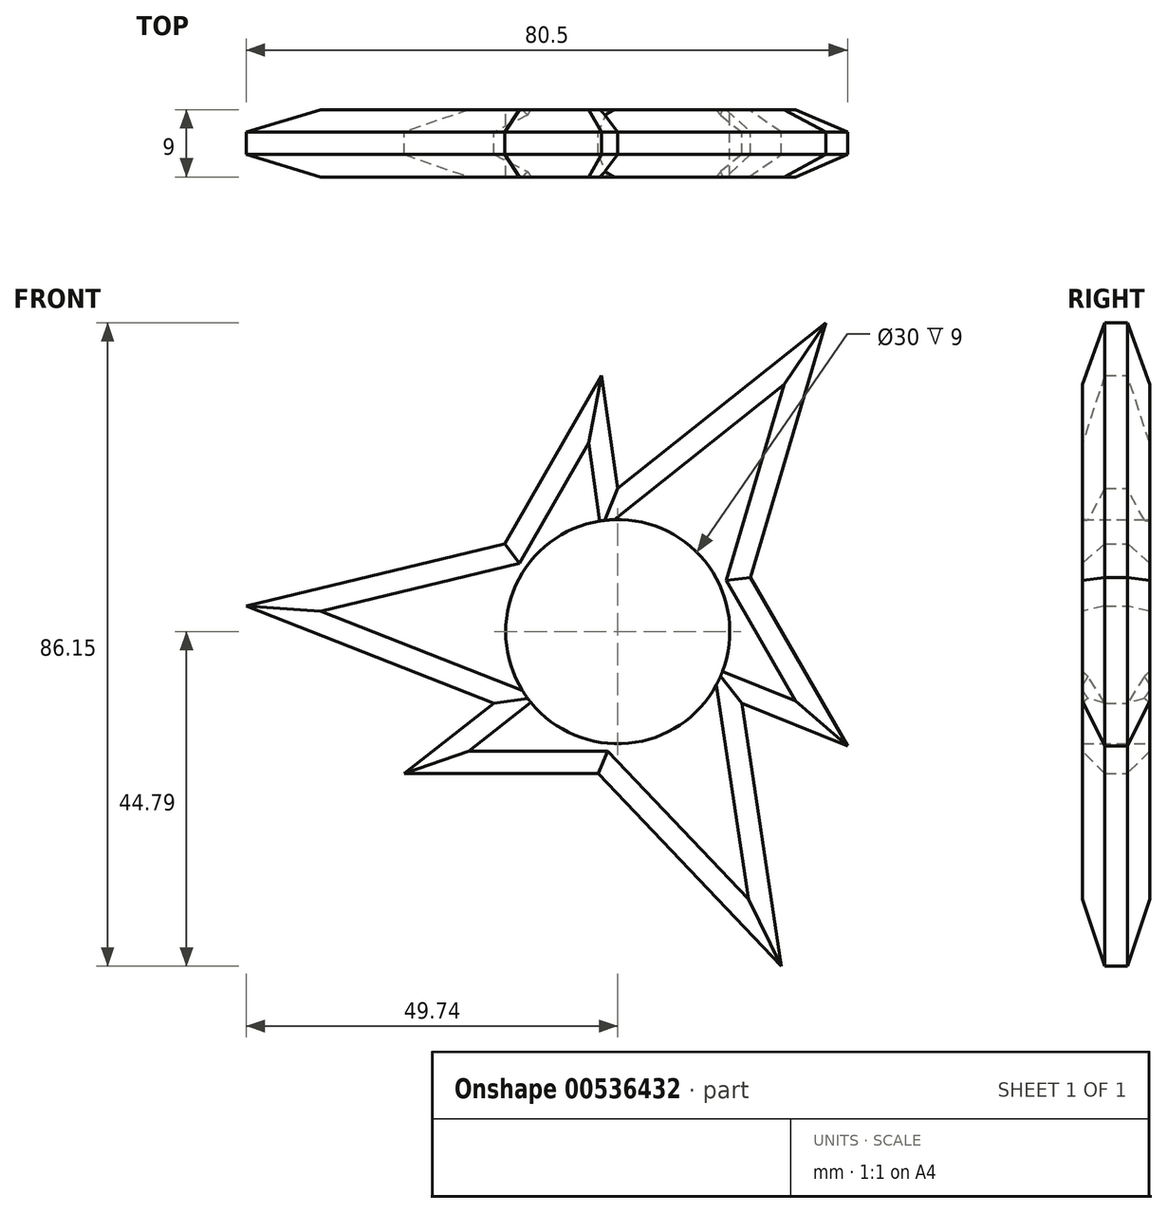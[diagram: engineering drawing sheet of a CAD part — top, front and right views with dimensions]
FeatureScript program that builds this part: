
annotation { "Feature Type Name" : "Feature", "Feature Type Description" : "" }
export const myFeature = defineFeature(function(context is Context, id is Id, definition is map)
    precondition{}
    {
        {
            var Q0;
            Q0=qCreatedBy(makeId("Front.planeOp"),FACE);
            var sketch = newSketch(context, id + "F0", { "sketchPlane" : qUnion([Q0])});
            skCircle(sketch, "E0", {"center": v(0, 0) * mm, "radius": 15 * mm});
            skCircle(sketch, "E1", {"center": v(0, 0) * mm, "radius": 19.18 * mm});
            skLineSegment(sketch, "E2", {"start": v(0, 19.18) * mm, "end": v(27.83, 41.36) * mm});
            skLineSegment(sketch, "E3", {"start": v(27.83, 41.36) * mm, "end": v(17.77, 7.22) * mm});
            skLineSegment(sketch, "E4.1.0", {"start": v(-16.61, -9.6) * mm, "end": v(-49.74, 3.42) * mm});
            skLineSegment(sketch, "E4.1.1", {"start": v(-49.74, 3.42) * mm, "end": v(-15.14, 11.78) * mm});
            skLineSegment(sketch, "E4.2.0", {"start": v(16.61, -9.6) * mm, "end": v(21.9, -44.79) * mm});
            skLineSegment(sketch, "E4.2.1", {"start": v(21.9, -44.79) * mm, "end": v(-2.63, -19) * mm});
            skLineSegment(sketch, "E5", {"start": v(-16.61, -9.6) * mm, "end": v(-28.62, -19) * mm});
            skLineSegment(sketch, "E6", {"start": v(-28.62, -19) * mm, "end": v(-2.63, -19) * mm});
            skLineSegment(sketch, "E7.1.0", {"start": v(16.61, -9.6) * mm, "end": v(30.76, -15.28) * mm});
            skLineSegment(sketch, "E7.1.1", {"start": v(30.76, -15.28) * mm, "end": v(17.77, 7.22) * mm});
            skLineSegment(sketch, "E7.2.0", {"start": v(0, 19.18) * mm, "end": v(-2.15, 34.28) * mm});
            skLineSegment(sketch, "E7.2.1", {"start": v(-2.15, 34.28) * mm, "end": v(-15.14, 11.78) * mm});
            skSolve(sketch);
        }
        {
            var Q0;
            {var subQ0=sQuery(id+"F0.wireOp",EDGE,"E4.1.0");Q0=makeQuery(id+"F0.imprint","IMPRINT",FACE,{"disambiguationData":[TD([[makeQuery(id+"F0.imprint","IMPRINT",EDGE,{"derivedFrom":subQ0}),-1.0]])]});}
            var Q1;
            {var subQ0=sQuery(id+"F0.wireOp",EDGE,"E2");Q1=makeQuery(id+"F0.imprint","IMPRINT",FACE,{"disambiguationData":[TD([[makeQuery(id+"F0.imprint","IMPRINT",EDGE,{"derivedFrom":subQ0}),-1.0]])]});}
            var Q2;
            {var subQ0=sQuery(id+"F0.wireOp",EDGE,"E4.2.0");Q2=makeQuery(id+"F0.imprint","IMPRINT",FACE,{"disambiguationData":[TD([[makeQuery(id+"F0.imprint","IMPRINT",EDGE,{"derivedFrom":subQ0}),-1.0]])]});}
            var Q3;
            Q3=makeQuery(id+"F0.imprint","IMPRINT",FACE,{"disambiguationData":[TD([[makeQuery(id+"F0.imprint","IMPRINT",EDGE,{"derivedFrom":sQuery(id+"F0.wireOp",EDGE,"E0")}),-1.0]])]});
            extrude(context, id + "F1", {"entities" : qUnion([Q0, Q1, Q2, Q3]), "depth" : 9 * mm, "offsetDistance" : 25 * mm});
        }
        {
            var Q0;
            Q0 = qSketchRegion(id + "F0", true);
            extrude(context, id + "F2", {"entities" : qUnion([Q0]), "operationType" : NewBodyOperationType.ADD, "depth" : 9 * mm, "offsetDistance" : 25 * mm});
        }
        {
            var Q0;
            Q0=makeQuery(id+"F2.opExtrude","CAP_EDGE",EDGE,{"disambiguationData":[OSD([sQuery(id+"F0.wireOp",EDGE,"E7.2.1")])],"isStart":false});
            var Q1;
            Q1=makeQuery(id+"F1.opExtrude","CAP_EDGE",EDGE,{"disambiguationData":[OSD([sQuery(id+"F0.wireOp",EDGE,"E4.1.1")])],"isStart":false});
            var Q2;
            Q2=makeQuery(id+"F1.opExtrude","CAP_EDGE",EDGE,{"disambiguationData":[OSD([sQuery(id+"F0.wireOp",EDGE,"E4.1.0")])],"isStart":false});
            var Q3;
            Q3=makeQuery(id+"F2.opExtrude","CAP_EDGE",EDGE,{"disambiguationData":[OSD([sQuery(id+"F0.wireOp",EDGE,"E5")])],"isStart":false});
            var Q4;
            Q4=makeQuery(id+"F2.opExtrude","CAP_EDGE",EDGE,{"disambiguationData":[OSD([sQuery(id+"F0.wireOp",EDGE,"E6")])],"isStart":false});
            var Q5;
            Q5=makeQuery(id+"F1.opExtrude","CAP_EDGE",EDGE,{"disambiguationData":[OSD([sQuery(id+"F0.wireOp",EDGE,"E4.2.1")])],"isStart":false});
            var Q6;
            Q6=makeQuery(id+"F1.opExtrude","CAP_EDGE",EDGE,{"disambiguationData":[OSD([sQuery(id+"F0.wireOp",EDGE,"E4.2.0")])],"isStart":false});
            var Q7;
            Q7=makeQuery(id+"F2.opExtrude","CAP_EDGE",EDGE,{"disambiguationData":[OSD([sQuery(id+"F0.wireOp",EDGE,"E7.1.0")])],"isStart":false});
            var Q8;
            Q8=makeQuery(id+"F2.opExtrude","CAP_EDGE",EDGE,{"disambiguationData":[OSD([sQuery(id+"F0.wireOp",EDGE,"E7.1.1")])],"isStart":false});
            var Q9;
            Q9=makeQuery(id+"F1.opExtrude","CAP_EDGE",EDGE,{"disambiguationData":[OSD([sQuery(id+"F0.wireOp",EDGE,"E3")])],"isStart":false});
            var Q10;
            Q10=makeQuery(id+"F1.opExtrude","CAP_EDGE",EDGE,{"disambiguationData":[OSD([sQuery(id+"F0.wireOp",EDGE,"E2")])],"isStart":false});
            var Q11;
            Q11=makeQuery(id+"F2.opExtrude","CAP_EDGE",EDGE,{"disambiguationData":[OSD([sQuery(id+"F0.wireOp",EDGE,"E7.2.0")])],"isStart":false});
            var Q12;
            Q12=makeQuery(id+"F1.opExtrude","CAP_EDGE",EDGE,{"disambiguationData":[OSD([sQuery(id+"F0.wireOp",EDGE,"E3")])],"isStart":true});
            var Q13;
            Q13=makeQuery(id+"F2.opExtrude","CAP_EDGE",EDGE,{"disambiguationData":[OSD([sQuery(id+"F0.wireOp",EDGE,"E7.1.1")])],"isStart":true});
            var Q14;
            Q14=makeQuery(id+"F1.opExtrude","CAP_EDGE",EDGE,{"disambiguationData":[OSD([sQuery(id+"F0.wireOp",EDGE,"E4.2.0")])],"isStart":true});
            var Q15;
            Q15=makeQuery(id+"F1.opExtrude","CAP_EDGE",EDGE,{"disambiguationData":[OSD([sQuery(id+"F0.wireOp",EDGE,"E4.2.1")])],"isStart":true});
            var Q16;
            Q16=makeQuery(id+"F2.opExtrude","CAP_EDGE",EDGE,{"disambiguationData":[OSD([sQuery(id+"F0.wireOp",EDGE,"E6")])],"isStart":true});
            var Q17;
            Q17=makeQuery(id+"F2.opExtrude","CAP_EDGE",EDGE,{"disambiguationData":[OSD([sQuery(id+"F0.wireOp",EDGE,"E5")])],"isStart":true});
            var Q18;
            Q18=makeQuery(id+"F1.opExtrude","CAP_EDGE",EDGE,{"disambiguationData":[OSD([sQuery(id+"F0.wireOp",EDGE,"E4.1.0")])],"isStart":true});
            var Q19;
            Q19=makeQuery(id+"F1.opExtrude","CAP_EDGE",EDGE,{"disambiguationData":[OSD([sQuery(id+"F0.wireOp",EDGE,"E4.1.1")])],"isStart":true});
            var Q20;
            Q20=makeQuery(id+"F2.opExtrude","CAP_EDGE",EDGE,{"disambiguationData":[OSD([sQuery(id+"F0.wireOp",EDGE,"E7.2.1")])],"isStart":true});
            var Q21;
            Q21=makeQuery(id+"F1.opExtrude","CAP_EDGE",EDGE,{"disambiguationData":[OSD([sQuery(id+"F0.wireOp",EDGE,"E2")])],"isStart":true});
            var Q22;
            Q22=makeQuery(id+"F2.opExtrude","CAP_EDGE",EDGE,{"disambiguationData":[OSD([sQuery(id+"F0.wireOp",EDGE,"E7.1.0")])],"isStart":true});
            var Q23;
            Q23=makeQuery(id+"F2.opExtrude","CAP_EDGE",EDGE,{"disambiguationData":[OSD([sQuery(id+"F0.wireOp",EDGE,"E7.2.0")])],"isStart":true});
            chamfer(context, id + "F3", {"entities" : qUnion([Q0, Q1, Q2, Q3, Q4, Q5, Q6, Q7, Q8, Q9, Q10, Q11, Q12, Q13, Q14, Q15, Q16, Q17, Q18, Q19, Q20, Q21, Q22, Q23]), "width" : 3 * mm, "tangentPropagation" : true});
        }
    });
